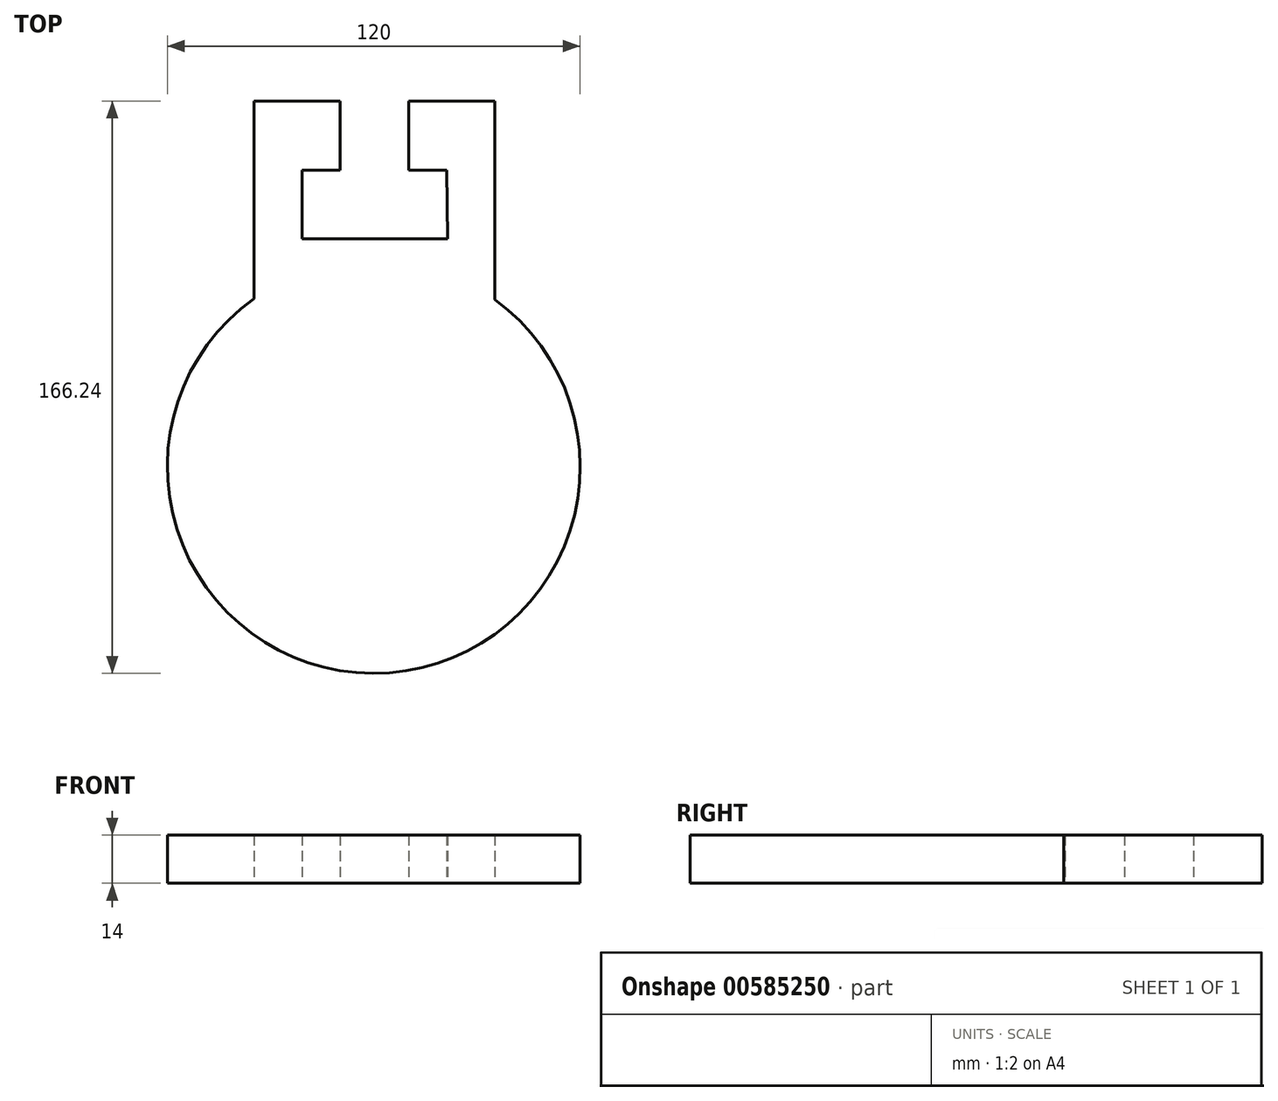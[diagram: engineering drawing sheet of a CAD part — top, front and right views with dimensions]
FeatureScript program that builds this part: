
annotation { "Feature Type Name" : "Feature", "Feature Type Description" : "" }
export const myFeature = defineFeature(function(context is Context, id is Id, definition is map)
    precondition{}
    {
        {
            var Q0;
            Q0=qCreatedBy(makeId("Top.planeOp"),FACE);
            var sketch = newSketch(context, id + "F0", { "sketchPlane" : qUnion([Q0])});
            skCircle(sketch, "E0", {"center": v(-0.19, -70.49) * mm, "radius": 60 * mm});
            skLineSegment(sketch, "E1.bottom", {"start": v(-34.99, -4.25) * mm, "end": v(35.01, -4.25) * mm});
            skLineSegment(sketch, "E1.top", {"start": v(-34.99, -21.9) * mm, "end": v(35.01, -21.9) * mm});
            skLineSegment(sketch, "E1.left", {"start": v(-34.99, -4.25) * mm, "end": v(-34.99, -21.9) * mm});
            skLineSegment(sketch, "E1.right", {"start": v(35.01, -4.25) * mm, "end": v(35.01, -21.9) * mm});
            skLineSegment(sketch, "E2", {"start": v(-34.99, -4.25) * mm, "end": v(-34.99, 35.75) * mm});
            skLineSegment(sketch, "E3", {"start": v(35.01, -4.25) * mm, "end": v(35.01, 35.75) * mm});
            skLineSegment(sketch, "E4", {"start": v(-34.99, 35.75) * mm, "end": v(-9.99, 35.75) * mm});
            skLineSegment(sketch, "E5", {"start": v(35.01, 35.75) * mm, "end": v(10.01, 35.75) * mm});
            skLineSegment(sketch, "E6", {"start": v(-9.99, 15.75) * mm, "end": v(-9.99, 35.75) * mm});
            skLineSegment(sketch, "E7", {"start": v(10.01, 35.75) * mm, "end": v(10.01, 15.75) * mm});
            skLineSegment(sketch, "E8", {"start": v(-9.99, 15.75) * mm, "end": v(-20.99, 15.75) * mm});
            skLineSegment(sketch, "E9", {"start": v(10.01, 15.75) * mm, "end": v(21.01, 15.75) * mm});
            skLineSegment(sketch, "E10", {"start": v(-20.99, 15.75) * mm, "end": v(-20.99, -4.25) * mm});
            skLineSegment(sketch, "E11", {"start": v(-20.99, -4.25) * mm, "end": v(21.21, -4.25) * mm});
            skLineSegment(sketch, "E12", {"start": v(21.01, 15.75) * mm, "end": v(21.21, -4.25) * mm});
            skSolve(sketch);
        }
        {
            var Q0;
            {var subQ0=sQuery(id+"F0.wireOp",EDGE,"E1.top");Q0=makeQuery(id+"F0.imprint","IMPRINT",FACE,{"disambiguationData":[TD([[makeQuery(id+"F0.imprint","IMPRINT",EDGE,{"derivedFrom":subQ0}),-1.0]])]});}
            var Q1;
            {var subQ0=sQuery(id+"F0.wireOp",EDGE,"E3");Q1=makeQuery(id+"F0.imprint","IMPRINT",FACE,{"disambiguationData":[TD([[makeQuery(id+"F0.imprint","IMPRINT",EDGE,{"derivedFrom":subQ0}),1.0]])]});}
            var Q2;
            {var subQ0=sQuery(id+"F0.wireOp",EDGE,"E2");Q2=makeQuery(id+"F0.imprint","IMPRINT",FACE,{"disambiguationData":[TD([[makeQuery(id+"F0.imprint","IMPRINT",EDGE,{"derivedFrom":subQ0}),-1.0]])]});}
            var Q3;
            {var subQ0=sQuery(id+"F0.wireOp",EDGE,"E1.top");Q3=makeQuery(id+"F0.imprint","IMPRINT",FACE,{"disambiguationData":[TD([[makeQuery(id+"F0.imprint","IMPRINT",EDGE,{"derivedFrom":subQ0}),1.0]])]});}
            var Q4;
            {var subQ0=sQuery(id+"F0.wireOp",EDGE,"E1.right");Q4=makeQuery(id+"F0.imprint","IMPRINT",FACE,{"disambiguationData":[TD([[makeQuery(id+"F0.imprint","IMPRINT",EDGE,{"derivedFrom":subQ0}),-1.0]])]});}
            extrude(context, id + "F1", {"entities" : qUnion([Q0, Q1, Q2, Q3, Q4]), "depth" : 14 * mm, "offsetDistance" : 25.4 * mm});
        }
    });
